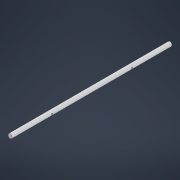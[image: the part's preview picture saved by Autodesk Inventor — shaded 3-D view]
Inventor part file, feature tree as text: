
AUTODESK INVENTOR PART (.ipt)
format: ipt  version: 2022 (Build 260153000, 153)  size: 105,472 bytes
history: native  units: in
note: dims shown in document units (in); Inventor stores cm internally (conversion verified against a paired STEP export)
features: extrude x1, fillet x1, sketch x1
ambient origin geometry x8: Origin, YZ Plane, XZ Plane, XY Plane, X Axis, Y Axis, Z Axis, Center Point
bodies: Solid1 (feature_tree)
feature tree (3):
  extrude  "Extrusion1"  Depth=0.5in
  fillet  "Fillet1"  Radius=0.3937in
  sketch  "Sketch1"  dims[d0=1.0in d1=39.3701in d3=0.3937in d4=1.0in d5=0.0in d6=0.5in]
